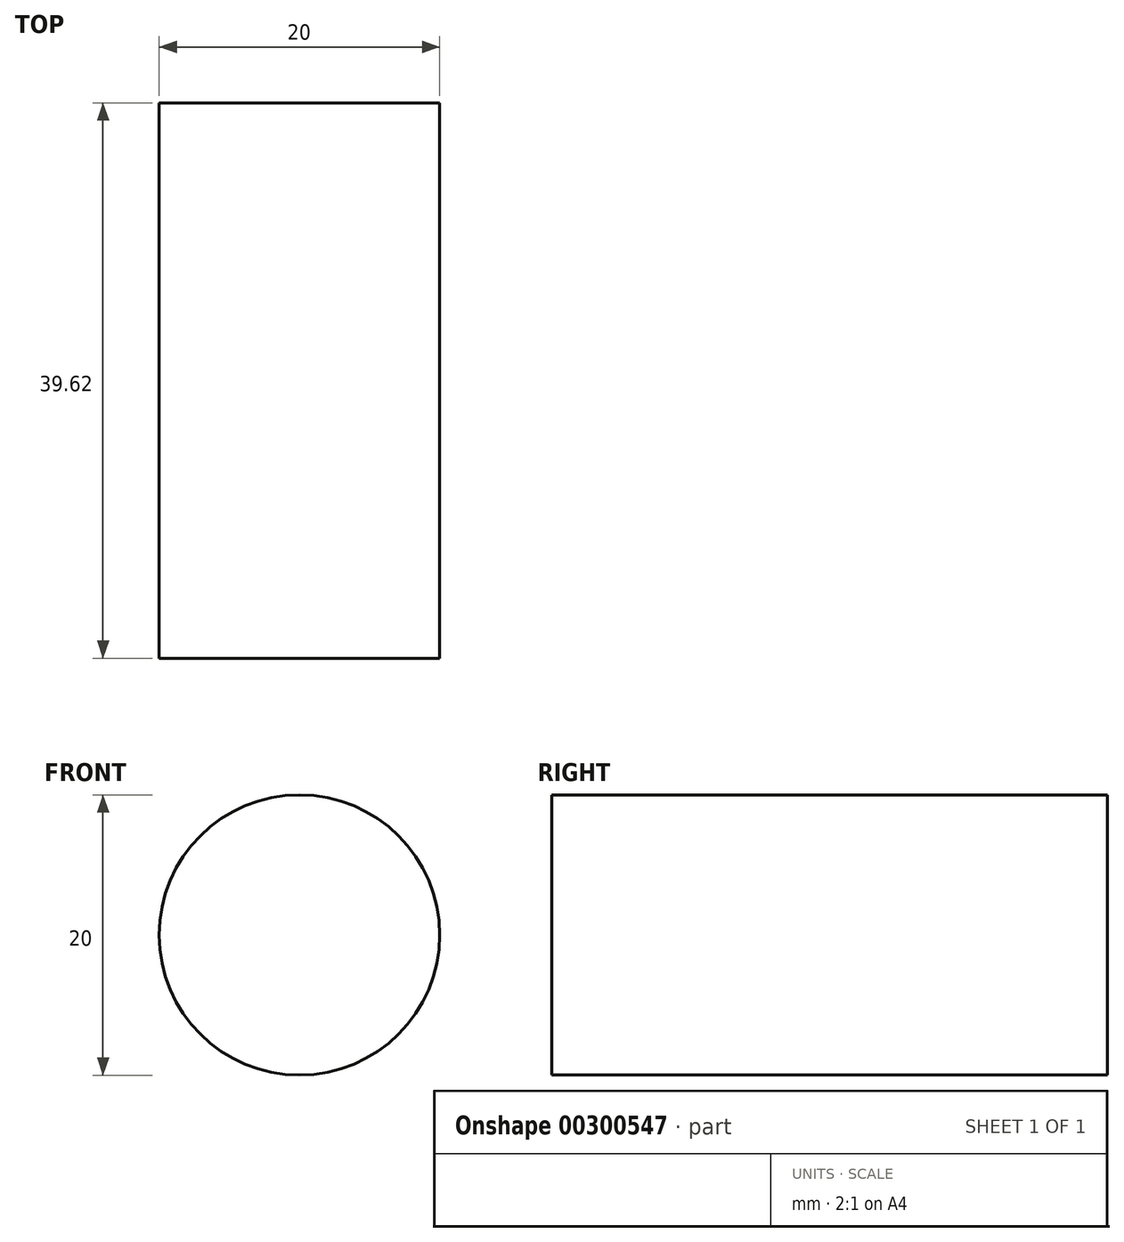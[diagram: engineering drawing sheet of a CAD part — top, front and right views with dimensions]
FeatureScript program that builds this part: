
annotation { "Feature Type Name" : "Feature", "Feature Type Description" : "" }
export const myFeature = defineFeature(function(context is Context, id is Id, definition is map)
    precondition{}
    {
        {
            var Q0;
            Q0=qCreatedBy(makeId("Front.planeOp"),FACE);
            var sketch = newSketch(context, id + "F0", { "sketchPlane" : qUnion([Q0])});
            skCircle(sketch, "E0", {"center": v(-144.18, 25.94) * mm, "radius": 10 * mm});
            skSolve(sketch);
        }
        {
            var Q0;
            Q0=makeQuery(id+"F0.imprint","IMPRINT",FACE,{"disambiguationData":[TD([[makeQuery(id+"F0.imprint","IMPRINT",EDGE,{"derivedFrom":sQuery(id+"F0.wireOp",EDGE,"E0")}),1.0]])]});
            extrude(context, id + "F1", {"entities" : qUnion([Q0]), "endBound" : BoundingType.SYMMETRIC, "depth" : 39.62 * mm});
        }
    });
